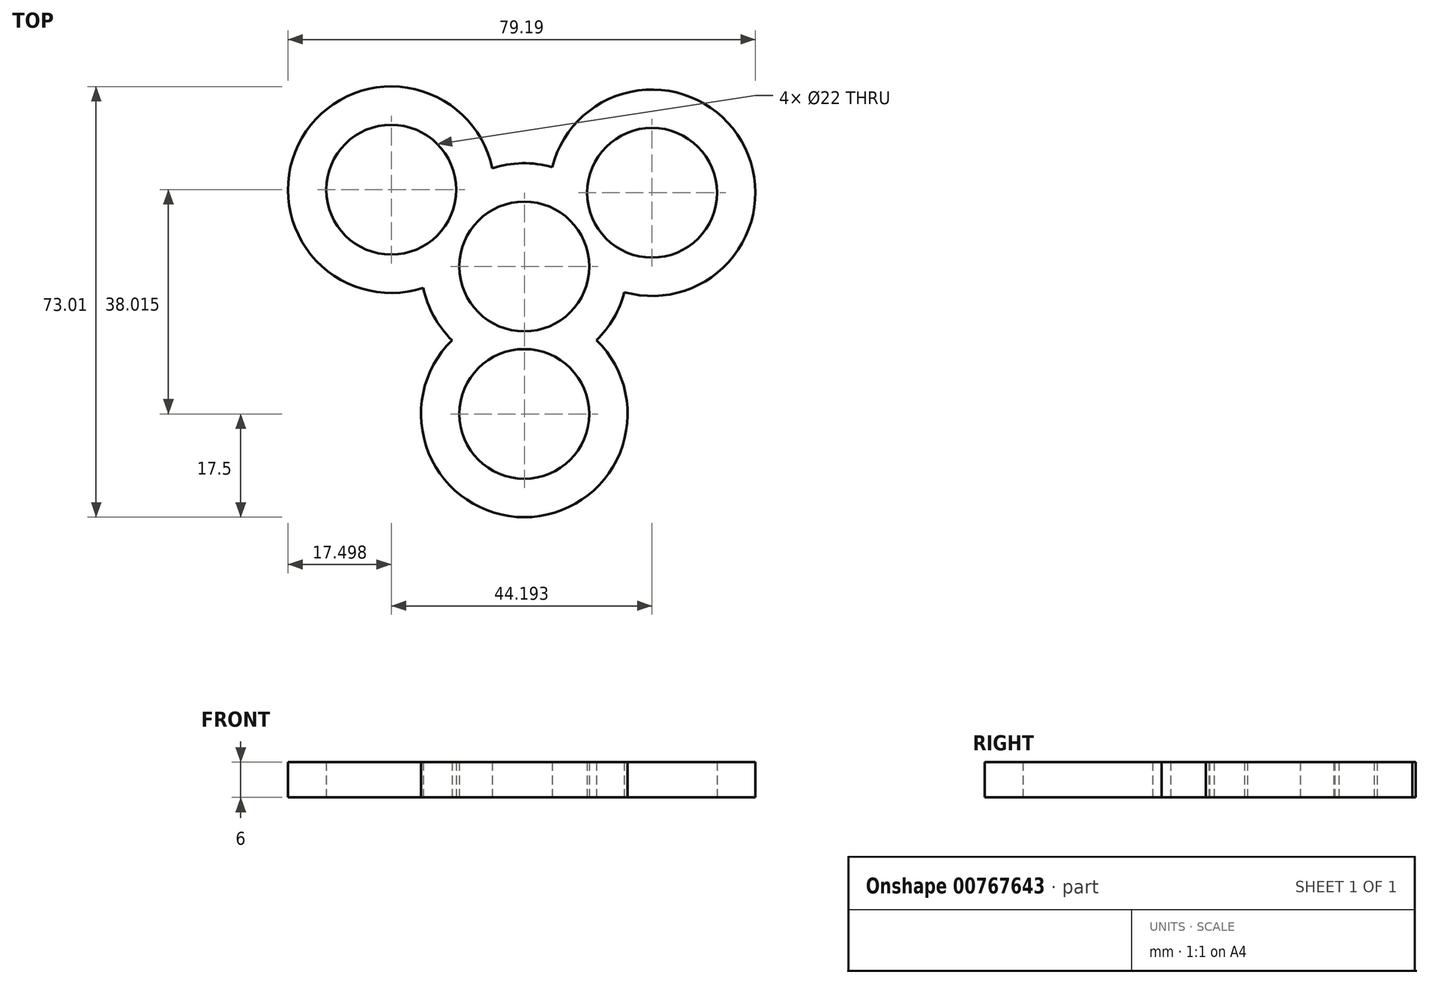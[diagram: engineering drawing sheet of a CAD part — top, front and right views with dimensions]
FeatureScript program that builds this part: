
annotation { "Feature Type Name" : "Feature", "Feature Type Description" : "" }
export const myFeature = defineFeature(function(context is Context, id is Id, definition is map)
    precondition{}
    {
        {
            var Q0;
            Q0=qCreatedBy(makeId("Top.planeOp"),FACE);
            var sketch = newSketch(context, id + "F0", { "sketchPlane" : qUnion([Q0])});
            skCircle(sketch, "E0", {"center": v(0, 0) * mm, "radius": 11 * mm});
            skCircle(sketch, "E1", {"center": v(0, -25) * mm, "radius": 11 * mm});
            skCircle(sketch, "E2", {"center": v(21.65, 12.5) * mm, "radius": 11 * mm});
            skCircle(sketch, "E3", {"center": v(-22.54, 13.01) * mm, "radius": 11 * mm});
            skArc(sketch, "E4", {"start": v(-5.42, 16.64) * mm, "mid": v(-37.7, 21.76) * mm, "end": v(-17.12, -3.62) * mm});
            skArc(sketch, "E5", {"start": v(-12.25, -12.5) * mm, "mid": v(0, -42.5) * mm, "end": v(12.25, -12.5) * mm});
            skArc(sketch, "E6", {"start": v(-17.12, -3.62) * mm, "mid": v(-15.34, -8.42) * mm, "end": v(-12.25, -12.5) * mm});
            skArc(sketch, "E7.trimOffspring", {"start": v(4.7, 16.86) * mm, "mid": v(-0.38, 17.5) * mm, "end": v(-5.42, 16.64) * mm});
            skArc(sketch, "E8.trimOffspring", {"start": v(16.95, -4.36) * mm, "mid": v(36.8, 21.25) * mm, "end": v(4.7, 16.86) * mm});
            skArc(sketch, "E9.trimOffspring", {"start": v(12.25, -12.5) * mm, "mid": v(15.16, -8.75) * mm, "end": v(16.95, -4.36) * mm});
            skSolve(sketch);
        }
        {
            var Q0;
            Q0=qSketchRegion(id+"F0",true);
            extrude(context, id + "F1", {"entities" : qUnion([Q0]), "depth" : 6 * mm, "offsetDistance" : 25 * mm});
        }
    });
